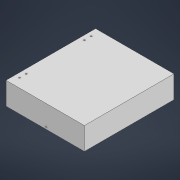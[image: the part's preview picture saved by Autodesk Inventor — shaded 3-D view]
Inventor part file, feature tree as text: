
AUTODESK INVENTOR PART (.ipt)
format: ipt  version: 2021 (Build 250183000, 183)  size: 140,288 bytes
history: native  units: mm
features: extrude x5, sketch x5
ambient origin geometry x8: Origin, YZ Plane, XZ Plane, XY Plane, X Axis, Y Axis, Z Axis, Center Point
bodies: Volumenkörper1 (feature_tree)
feature tree (10):
  extrude  "Extrusion1"  Depth=200.0mm
  extrude  "Extrusion2"  Depth=2.0mm
  extrude  "Extrusion3"  Depth=2.0mm
  extrude  "Extrusion4"  Depth=48.0mm
  extrude  "Extrusion5"  Depth=50.0mm
  sketch  "Skizze1"  dims[d0=175.0mm d1=200.0mm]
  sketch  "Skizze2"  dims[d2=2.0mm d3=0.0mm d4=2.0mm]
  sketch  "Skizze3"  dims[d5=2.0mm d6=2.0mm]
  sketch  "Skizze4"  dims[d7=48.0mm d8=0.0mm d9=3.2mm]
  sketch  "Skizze5"  dims[d10=3.2mm d11=3.2mm d12=3.2mm d13=10.0mm d14=10.0mm d15=15.0mm d16=20.0mm d17=10.0mm d18=10.0mm d19=20.0mm d20=15.0mm d21=2.0mm d22=0.0mm d23=3.2mm d24=85.0mm d25=5.0mm d26=50.0mm d27=0.0mm d28=3.2mm d29=5.0mm d30=85.0mm d31=50.0mm d32=0.0mm]
